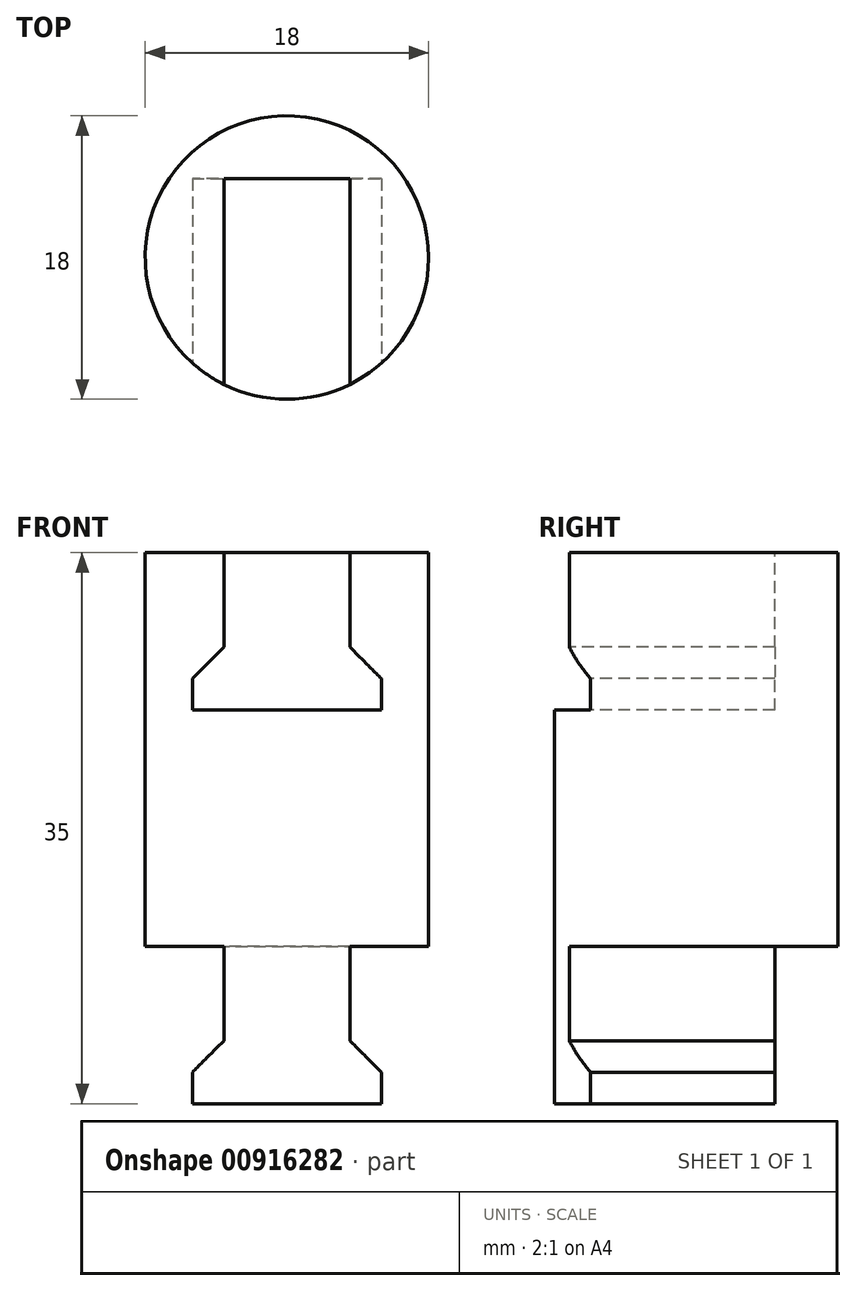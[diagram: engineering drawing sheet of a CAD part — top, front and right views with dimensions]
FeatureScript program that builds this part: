
annotation { "Feature Type Name" : "Feature", "Feature Type Description" : "" }
export const myFeature = defineFeature(function(context is Context, id is Id, definition is map)
    precondition{}
    {
        {
            var Q0;
            Q0=qCreatedBy(makeId("Top.planeOp"),FACE);
            var sketch = newSketch(context, id + "F0", { "sketchPlane" : qUnion([Q0])});
            skCircle(sketch, "E0", {"center": v(0, 0) * mm, "radius": 9 * mm});
            skSolve(sketch);
        }
        {
            var Q0;
            Q0 = qSketchRegion(id + "F0", true);
            extrude(context, id + "F1", {"entities" : qUnion([Q0]), "depth" : 20 * mm, "offsetDistance" : 25 * mm});
        }
        {
            var Q0;
            Q0=qCreatedBy(makeId("Front.planeOp"),FACE);
            var sketch = newSketch(context, id + "F2", { "sketchPlane" : qUnion([Q0])});
            skLineSegment(sketch, "E1", {"start": v(0, 20) * mm, "end": v(-4, 20) * mm});
            skLineSegment(sketch, "E2", {"start": v(-6, 10) * mm, "end": v(0, 10) * mm});
            skLineSegment(sketch, "E3", {"start": v(0, 10) * mm, "end": v(0, 20) * mm});
            skLineSegment(sketch, "E4", {"start": v(-6, 10) * mm, "end": v(-6, 12) * mm});
            skLineSegment(sketch, "E5", {"start": v(-6, 12) * mm, "end": v(-4, 12) * mm});
            skLineSegment(sketch, "E6", {"start": v(-4, 12) * mm, "end": v(-4, 20) * mm});
            skLineSegment(sketch, "E7.MirrorCS", {"start": v(0, 20) * mm, "end": v(4, 20) * mm});
            skLineSegment(sketch, "E8.MirrorCS", {"start": v(4, 12) * mm, "end": v(4, 20) * mm});
            skLineSegment(sketch, "E9.MirrorCS", {"start": v(6, 12) * mm, "end": v(4, 12) * mm});
            skLineSegment(sketch, "E10.MirrorCS", {"start": v(6, 10) * mm, "end": v(6, 12) * mm});
            skLineSegment(sketch, "E11.MirrorCS", {"start": v(6, 10) * mm, "end": v(0, 10) * mm});
            skLineSegment(sketch, "E12.0.1.0", {"start": v(0, -15) * mm, "end": v(0, -5) * mm});
            skLineSegment(sketch, "E12.0.1.1", {"start": v(-4, -13) * mm, "end": v(-4, -5) * mm});
            skLineSegment(sketch, "E12.0.1.2", {"start": v(4, -13) * mm, "end": v(4, -5) * mm});
            skLineSegment(sketch, "E12.0.1.3", {"start": v(0, -5) * mm, "end": v(4, -5) * mm});
            skLineSegment(sketch, "E12.0.1.4", {"start": v(0, -5) * mm, "end": v(-4, -5) * mm});
            skLineSegment(sketch, "E12.0.1.5", {"start": v(6, -15) * mm, "end": v(6, -13) * mm});
            skLineSegment(sketch, "E12.0.1.6", {"start": v(6, -13) * mm, "end": v(4, -13) * mm});
            skLineSegment(sketch, "E12.0.1.7", {"start": v(6, -15) * mm, "end": v(0, -15) * mm});
            skLineSegment(sketch, "E12.0.1.8", {"start": v(-6, -15) * mm, "end": v(0, -15) * mm});
            skLineSegment(sketch, "E12.0.1.9", {"start": v(-6, -15) * mm, "end": v(-6, -13) * mm});
            skLineSegment(sketch, "E12.0.1.10", {"start": v(-6, -13) * mm, "end": v(-4, -13) * mm});
            skLineSegment(sketch, "E12.direction1", {"start": v(0, 10) * mm, "end": v(0, 10) * mm});
            skLineSegment(sketch, "E12.direction2", {"start": v(0, 10) * mm, "end": v(0, -15) * mm, "construction": true});
            skLineSegment(sketch, "E13", {"start": v(-4, -5) * mm, "end": v(-9, -5) * mm});
            skLineSegment(sketch, "E14", {"start": v(-9, -5) * mm, "end": v(-9, -15) * mm});
            skLineSegment(sketch, "E15", {"start": v(-9, -15) * mm, "end": v(-6, -15) * mm});
            skLineSegment(sketch, "E16.MirrorCS", {"start": v(9, -15) * mm, "end": v(6, -15) * mm});
            skLineSegment(sketch, "E17.MirrorCS", {"start": v(9, -5) * mm, "end": v(9, -15) * mm});
            skLineSegment(sketch, "E18.MirrorCS", {"start": v(4, -5) * mm, "end": v(9, -5) * mm});
            skSolve(sketch);
        }
        {
            var Q0;
            Q0 = qSketchRegion(id + "F2", true);
            extrude(context, id + "F3", {"entities" : qUnion([Q0]), "operationType" : NewBodyOperationType.REMOVE, "oppositeDirection" : true, "depth" : 5 * mm, "offsetDistance" : 25 * mm, "hasSecondDirection" : true, "secondDirectionOppositeDirection" : false, "secondDirectionDepth" : 25 * mm});
        }
        {
            var Q0;
            Q0=makeQuery(id+"F1.opExtrude","CAP_FACE",FACE,{"disambiguationData":[OSD([sQuery(id+"F0.wireOp",EDGE,"E0")])],"isStart":true});
            extrude(context, id + "F4", {"entities" : qUnion([Q0]), "operationType" : NewBodyOperationType.ADD, "depth" : 15 * mm, "offsetDistance" : 25 * mm});
        }
        {
            var Q0;
            Q0=makeQuery(id+"F2.imprint","IMPRINT",FACE,{"disambiguationData":[TD([[makeQuery(id+"F2.imprint","IMPRINT",EDGE,{"derivedFrom":sQuery(id+"F2.wireOp",EDGE,"E12.0.1.1")}),1.0]])]});
            var Q1;
            Q1=makeQuery(id+"F2.imprint","IMPRINT",FACE,{"disambiguationData":[TD([[makeQuery(id+"F2.imprint","IMPRINT",EDGE,{"derivedFrom":sQuery(id+"F2.wireOp",EDGE,"E12.0.1.2")}),-1.0]])]});
            extrude(context, id + "F5", {"entities" : qUnion([Q0, Q1]), "operationType" : NewBodyOperationType.REMOVE, "oppositeDirection" : true, "depth" : 25 * mm, "offsetDistance" : 25 * mm, "hasSecondDirection" : true, "secondDirectionOppositeDirection" : false, "secondDirectionDepth" : 25 * mm});
        }
        {
            var Q0;
            Q0=makeQuery(id+"F4.opExtrude","CAP_FACE",FACE,{"disambiguationData":[OSD([sQuery(id+"F0.wireOp",EDGE,"E0")])],"isStart":false});
            var sketch = newSketch(context, id + "F6", { "sketchPlane" : qUnion([Q0])});
            skLineSegment(sketch, "E19.bottom", {"start": v(6.9, -5) * mm, "end": v(-6.9, -5) * mm});
            skLineSegment(sketch, "E19.top", {"start": v(6.9, -13) * mm, "end": v(-6.9, -13) * mm});
            skLineSegment(sketch, "E19.left", {"start": v(6.9, -5) * mm, "end": v(6.9, -13) * mm});
            skLineSegment(sketch, "E19.right", {"start": v(-6.9, -5) * mm, "end": v(-6.9, -13) * mm});
            skPoint(sketch, "E19.middle", {"position": v(0, -9) * mm});
            skSolve(sketch);
        }
        {
            var Q0;
            Q0 = qSketchRegion(id + "F6", true);
            extrude(context, id + "F7", {"entities" : qUnion([Q0]), "operationType" : NewBodyOperationType.REMOVE, "oppositeDirection" : true, "depth" : 10 * mm, "offsetDistance" : 25 * mm});
        }
        {
            var Q0;
            Q0=makeQuery(id+"F3.boolean.opBoolean","COPY",EDGE,{"derivedFrom":makeQuery(id+"F3.opExtrude","SWEPT_EDGE",EDGE,{"disambiguationData":[OSD([sQuery(id+"F2.wireOp",EDGE,"E8.MirrorCS"),sQuery(id+"F2.wireOp",EDGE,"E9.MirrorCS")])]})});
            var Q1;
            Q1=makeQuery(id+"F3.boolean.opBoolean","COPY",EDGE,{"derivedFrom":makeQuery(id+"F3.opExtrude","SWEPT_EDGE",EDGE,{"disambiguationData":[OSD([sQuery(id+"F2.wireOp",EDGE,"E5"),sQuery(id+"F2.wireOp",EDGE,"E6")])]})});
            var Q2;
            Q2=makeQuery(id+"F5.boolean.opBoolean","COPY",EDGE,{"derivedFrom":makeQuery(id+"F5.opExtrude","SWEPT_EDGE",EDGE,{"disambiguationData":[OSD([sQuery(id+"F2.wireOp",EDGE,"E12.0.1.1"),sQuery(id+"F2.wireOp",EDGE,"E12.0.1.10")])]})});
            var Q3;
            Q3=makeQuery(id+"F5.boolean.opBoolean","COPY",EDGE,{"derivedFrom":makeQuery(id+"F5.opExtrude","SWEPT_EDGE",EDGE,{"disambiguationData":[OSD([sQuery(id+"F2.wireOp",EDGE,"E12.0.1.2"),sQuery(id+"F2.wireOp",EDGE,"E12.0.1.6")])]})});
            chamfer(context, id + "F8", {"entities" : qUnion([Q0, Q1, Q2, Q3]), "chamferType" : ChamferType.OFFSET_ANGLE, "width" : 2 * mm, "oppositeDirection" : false, "angle" : 45 * degree, "tangentPropagation" : true});
        }
    });
